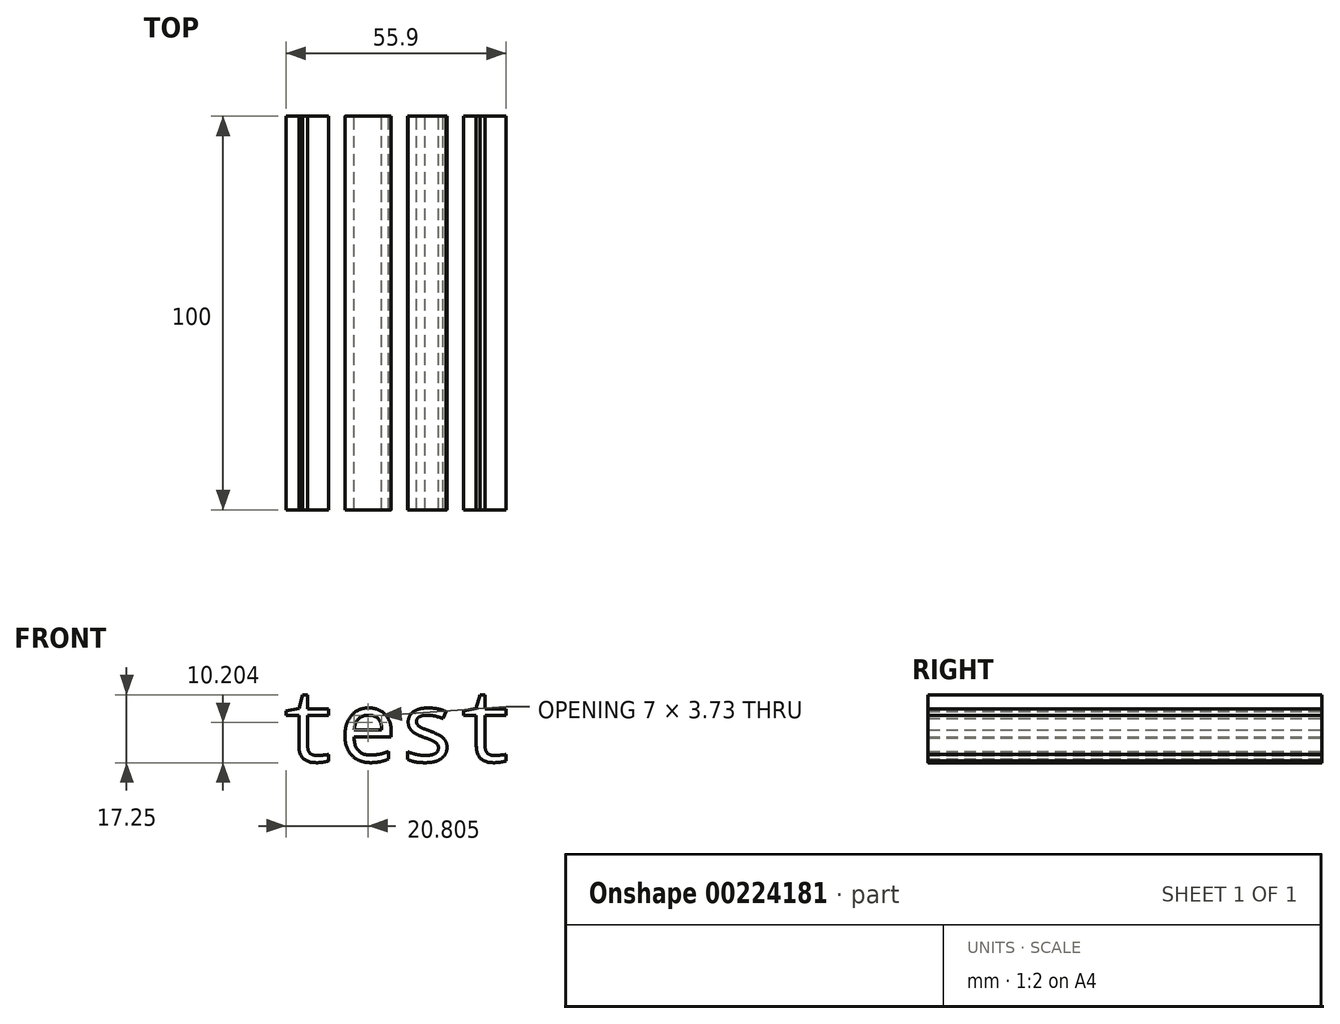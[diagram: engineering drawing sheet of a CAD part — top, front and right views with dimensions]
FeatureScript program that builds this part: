
annotation { "Feature Type Name" : "Feature", "Feature Type Description" : "" }
export const myFeature = defineFeature(function(context is Context, id is Id, definition is map)
    precondition{}
    {
        {
            var Q0;
            Q0=qCreatedBy(makeId("Front.planeOp"),FACE);
            var sketch = newSketch(context, id + "F0", { "sketchPlane" : qUnion([Q0])});
            skText(sketch, "E0", { "text": "test", "fontName": "DroidSansMono.ttf"});
            const initialGuessF0  = {"E0": [-0.00956, 0.10448, 1, 0, 0.01802]};
            skSetInitialGuess(sketch, initialGuessF0);
            skSolve(sketch);
        }
        {
            var Q0;
            Q0 = qSketchRegion(id + "F0", true);
            extrude(context, id + "F1", {"entities" : qUnion([Q0]), "endBound" : BoundingType.SYMMETRIC, "depth" : 100 * mm});
        }
    });
